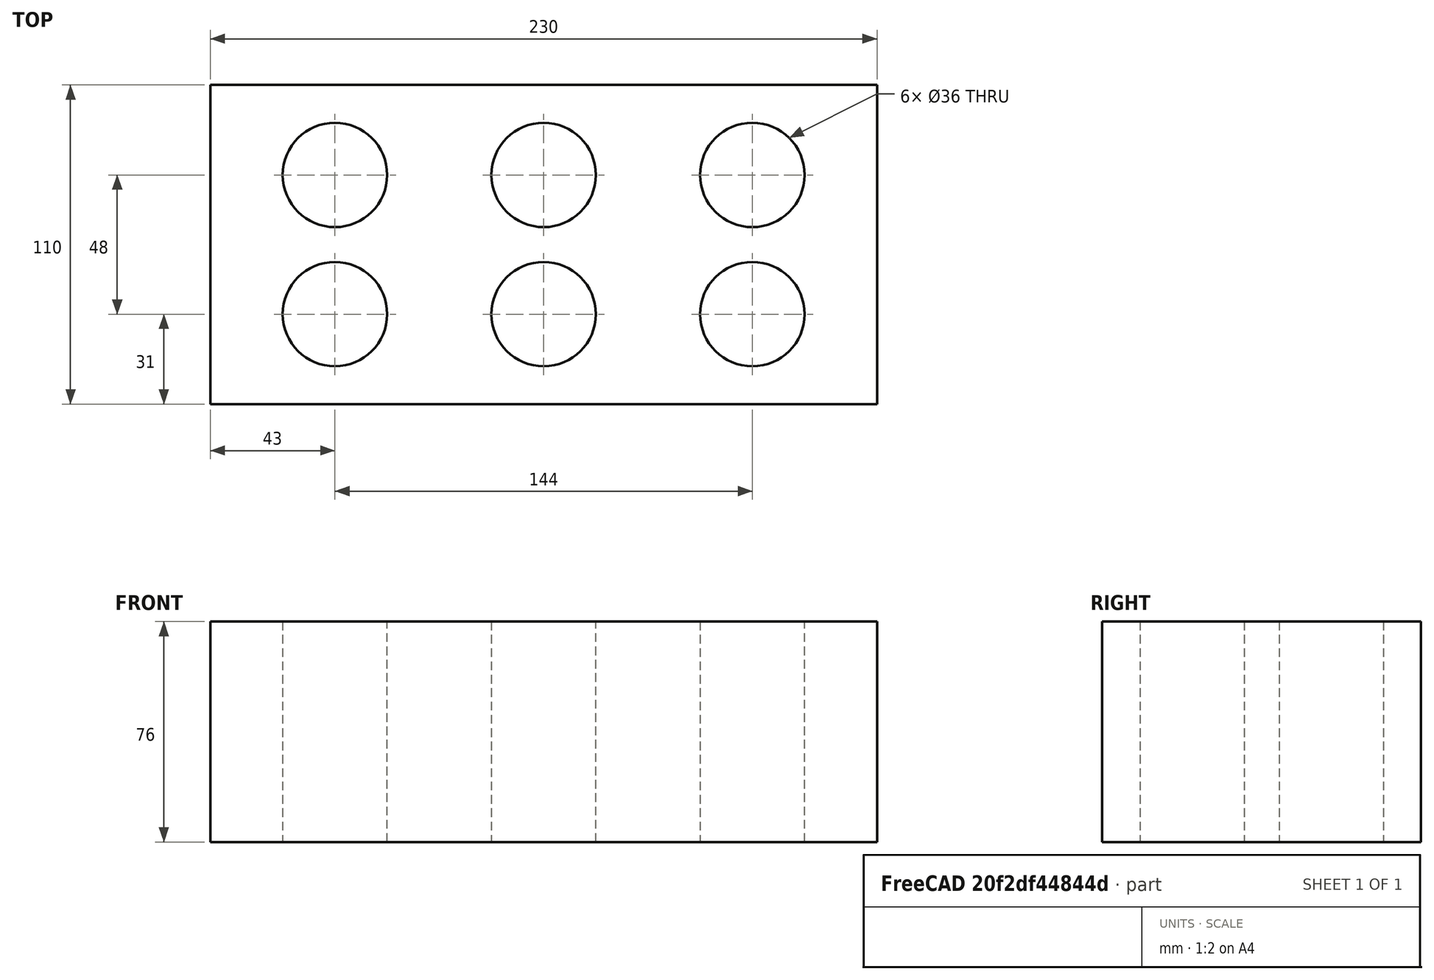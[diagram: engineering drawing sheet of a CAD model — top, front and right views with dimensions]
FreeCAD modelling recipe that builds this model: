
FCSTD DOCUMENT  (FreeCAD 0.21R33694 (Git))
Label: OJT1_T09R02_maó
License: All rights reserved
LicenseURL: http://en.wikipedia.org/wiki/All_rights_reserved
objects: Part::Cylinder×6, Part::Box×1, Part::MultiFuse×1, Part::Cut×1
note: 9 computed .brp shape members not serialized (recipe doc carries the construction recipe); baked Part::Feature solids carry a one-line shape summary decoded from their .brp

FEATURE [Part::Box] Box  label="base"
  AttacherType = Attacher::AttachEngine3D
  Height = 76
  Length = 230
  Placement = pos=(-43,-31,0) rot=(0,0,1;0rad)
  Width = 110
FEATURE [Part::Cylinder] Cylinder  label="cercle1"
  Angle = 360
  AttacherType = Attacher::AttachEngine3D
  FirstAngle = 0
  Height = 76
  Radius = 18
  SecondAngle = 0
FEATURE [Part::Cylinder] Cylinder001  label="cercle2"
  Angle = 360
  AttacherType = Attacher::AttachEngine3D
  FirstAngle = 0
  Height = 76
  Placement = pos=(72,0,0) rot=(0,0,1;0rad)
  Radius = 18
  SecondAngle = 0
FEATURE [Part::Cylinder] Cylinder002  label="cercle3"
  Angle = 360
  AttacherType = Attacher::AttachEngine3D
  FirstAngle = 0
  Height = 76
  Placement = pos=(144,0,0) rot=(0,0,1;0rad)
  Radius = 18
  SecondAngle = 0
FEATURE [Part::Cylinder] Cylinder003  label="cercle4"
  Angle = 360
  AttacherType = Attacher::AttachEngine3D
  FirstAngle = 0
  Height = 76
  Placement = pos=(0,48,0) rot=(0,0,1;0rad)
  Radius = 18
  SecondAngle = 0
FEATURE [Part::Cylinder] Cylinder004  label="cercle5"
  Angle = 360
  AttacherType = Attacher::AttachEngine3D
  FirstAngle = 0
  Height = 76
  Placement = pos=(72,48,0) rot=(0,0,1;0rad)
  Radius = 18
  SecondAngle = 0
FEATURE [Part::Cylinder] Cylinder005  label="cercle6"
  Angle = 360
  AttacherType = Attacher::AttachEngine3D
  FirstAngle = 0
  Height = 76
  Placement = pos=(144,48,0) rot=(0,0,1;0rad)
  Radius = 18
  SecondAngle = 0
FEATURE [Part::MultiFuse] Fusion
  Refine = true
  Shapes = -> [Cylinder005,Cylinder,Cylinder001,Cylinder002,Cylinder003,Cylinder004]
FEATURE [Part::Cut] Cut  label="Maó"
  Base = -> Box
  Refine = true
  Tool = -> Fusion
